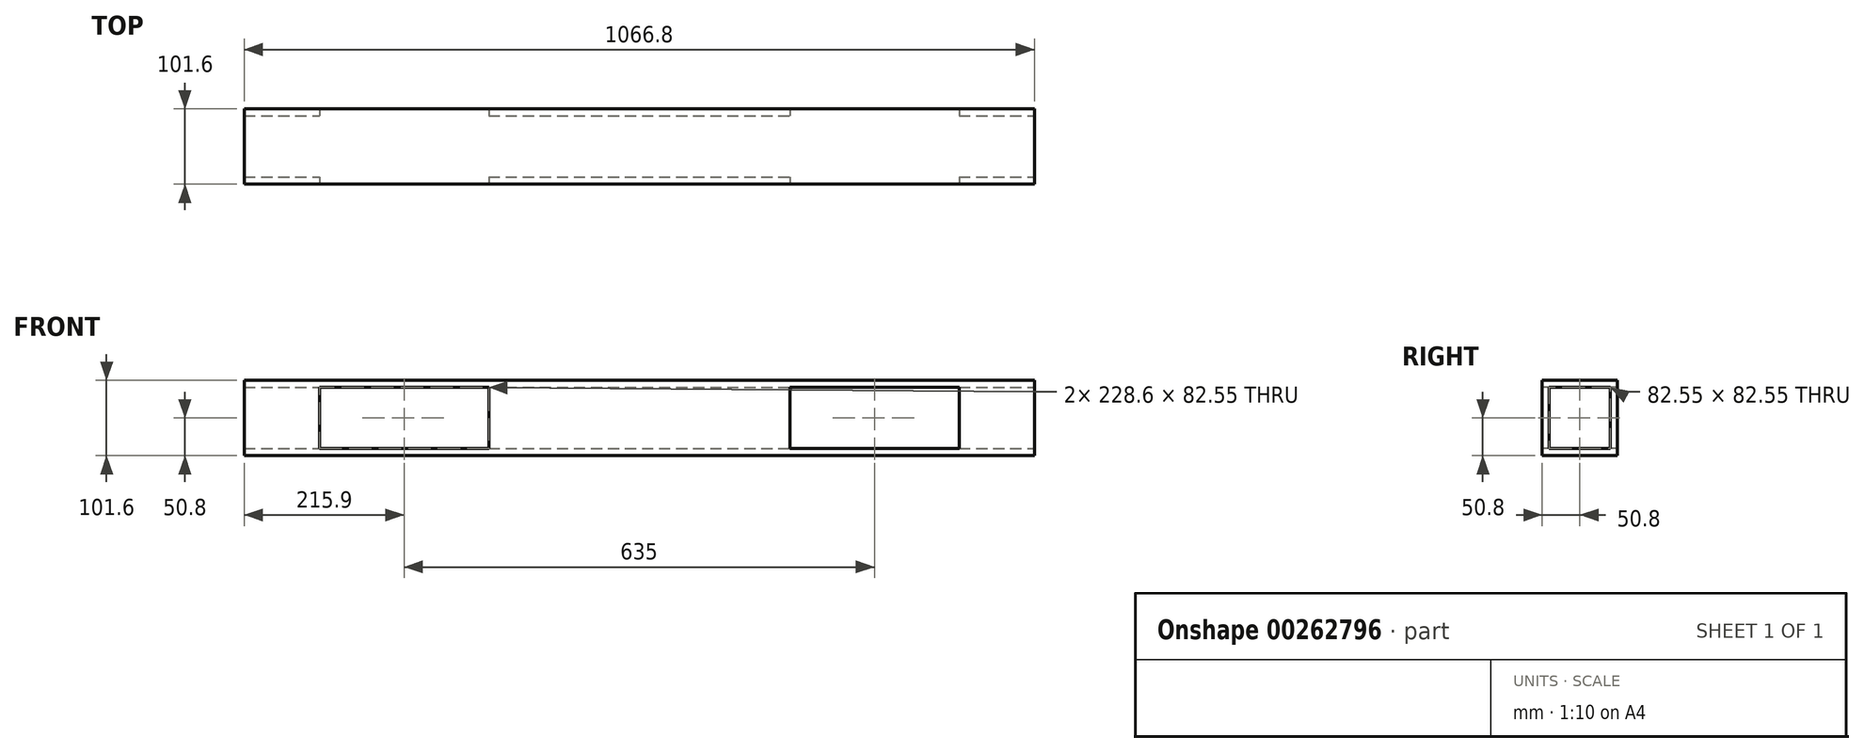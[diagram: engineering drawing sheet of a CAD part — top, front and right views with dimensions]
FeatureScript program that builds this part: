
annotation { "Feature Type Name" : "Feature", "Feature Type Description" : "" }
export const myFeature = defineFeature(function(context is Context, id is Id, definition is map)
    precondition{}
    {
        {
            var Q0;
            Q0=qCreatedBy(makeId("Top.planeOp"),FACE);
            var sketch = newSketch(context, id + "F0", { "sketchPlane" : qUnion([Q0])});
            skLineSegment(sketch, "E0.bottom", {"start": v(-533.4, -50.8) * mm, "end": v(533.4, -50.8) * mm});
            skLineSegment(sketch, "E0.top", {"start": v(-533.4, 50.8) * mm, "end": v(533.4, 50.8) * mm});
            skLineSegment(sketch, "E0.left", {"start": v(-533.4, -50.8) * mm, "end": v(-533.4, 50.8) * mm});
            skLineSegment(sketch, "E0.right", {"start": v(533.4, -50.8) * mm, "end": v(533.4, 50.8) * mm});
            skPoint(sketch, "E0.middle", {"position": v(0, 0) * mm});
            skSolve(sketch);
        }
        {
            var Q0;
            Q0=makeQuery(id+"F0.imprint","IMPRINT",FACE,{"disambiguationData":[TD([[makeQuery(id+"F0.imprint","IMPRINT",EDGE,{"derivedFrom":sQuery(id+"F0.wireOp",EDGE,"E0.bottom")}),1.0]])]});
            extrude(context, id + "F1", {"entities" : qUnion([Q0]), "endBound" : BoundingType.SYMMETRIC, "depth" : 101.6 * mm});
        }
        {
            var Q0;
            Q0=makeQuery(id+"F1.opExtrude","SWEPT_FACE",FACE,{"disambiguationData":[OSD([sQuery(id+"F0.wireOp",EDGE,"E0.right")])]});
            var sketch = newSketch(context, id + "F2", { "sketchPlane" : qUnion([Q0])});
            skLineSegment(sketch, "E1.0", {"start": v(-41.28, 41.28) * mm, "end": v(41.27, 41.28) * mm});
            skLineSegment(sketch, "E1.1", {"start": v(-41.28, 41.28) * mm, "end": v(-41.28, -41.28) * mm});
            skLineSegment(sketch, "E1.2", {"start": v(-41.28, -41.28) * mm, "end": v(41.27, -41.28) * mm});
            skLineSegment(sketch, "E1.3", {"start": v(41.27, 41.28) * mm, "end": v(41.27, -41.28) * mm});
            skSolve(sketch);
        }
        {
            var Q0;
            Q0=makeQuery(id+"F2.imprint","IMPRINT",FACE,{"disambiguationData":[TD([[makeQuery(id+"F2.imprint","IMPRINT",EDGE,{"derivedFrom":sQuery(id+"F2.wireOp",EDGE,"E1.0")}),-1.0]])]});
            extrude(context, id + "F3", {"entities" : qUnion([Q0]), "operationType" : NewBodyOperationType.REMOVE, "endBound" : BoundingType.THROUGH_ALL, "oppositeDirection" : true, "depth" : 25.4 * mm});
        }
        {
            var Q0;
            Q0=makeQuery(id+"F1.opExtrude","SWEPT_FACE",FACE,{"disambiguationData":[OSD([sQuery(id+"F0.wireOp",EDGE,"E0.bottom")])]});
            var sketch = newSketch(context, id + "F4", { "sketchPlane" : qUnion([Q0])});
            skLineSegment(sketch, "E2.bottom", {"start": v(-203.2, 50.8) * mm, "end": v(203.2, 50.8) * mm});
            skLineSegment(sketch, "E2.top", {"start": v(-203.2, -50.8) * mm, "end": v(203.2, -50.8) * mm});
            skLineSegment(sketch, "E2.left", {"start": v(-203.2, 50.8) * mm, "end": v(-203.2, -50.8) * mm});
            skLineSegment(sketch, "E2.right", {"start": v(203.2, 50.8) * mm, "end": v(203.2, -50.8) * mm});
            skPoint(sketch, "E2.middle", {"position": v(0, 0) * mm});
            skLineSegment(sketch, "E3.bottom", {"start": v(-203.2, -50.8) * mm, "end": v(-431.8, -50.8) * mm});
            skLineSegment(sketch, "E3.top", {"start": v(-203.2, 50.8) * mm, "end": v(-431.8, 50.8) * mm});
            skLineSegment(sketch, "E3.left", {"start": v(-203.2, -50.8) * mm, "end": v(-203.2, 50.8) * mm});
            skLineSegment(sketch, "E3.right", {"start": v(-431.8, -50.8) * mm, "end": v(-431.8, 50.8) * mm});
            skLineSegment(sketch, "E4.bottom", {"start": v(203.2, -50.8) * mm, "end": v(431.8, -50.8) * mm});
            skLineSegment(sketch, "E4.top", {"start": v(203.2, 50.8) * mm, "end": v(431.8, 50.8) * mm});
            skLineSegment(sketch, "E4.left", {"start": v(203.2, -50.8) * mm, "end": v(203.2, 50.8) * mm});
            skLineSegment(sketch, "E4.right", {"start": v(431.8, -50.8) * mm, "end": v(431.8, 50.8) * mm});
            skLineSegment(sketch, "E5.0", {"start": v(-203.2, 41.28) * mm, "end": v(-431.8, 41.28) * mm});
            skLineSegment(sketch, "E5.2", {"start": v(-203.2, -41.28) * mm, "end": v(-431.8, -41.28) * mm});
            skLineSegment(sketch, "E6.1", {"start": v(203.2, -41.27) * mm, "end": v(431.8, -41.27) * mm});
            skLineSegment(sketch, "E6.3", {"start": v(203.2, 41.27) * mm, "end": v(431.8, 41.27) * mm});
            skSolve(sketch);
        }
        {
            var Q0;
            {var subQ0=sQuery(id+"F4.wireOp",EDGE,"E5.0");Q0=makeQuery(id+"F4.imprint","IMPRINT",FACE,{"disambiguationData":[TD([[makeQuery(id+"F4.imprint","IMPRINT",EDGE,{"derivedFrom":subQ0}),1.0]])]});}
            var Q1;
            {var subQ0=sQuery(id+"F4.wireOp",EDGE,"E6.1");Q1=makeQuery(id+"F4.imprint","IMPRINT",FACE,{"disambiguationData":[TD([[makeQuery(id+"F4.imprint","IMPRINT",EDGE,{"derivedFrom":subQ0}),1.0]])]});}
            extrude(context, id + "F5", {"entities" : qUnion([Q0, Q1]), "operationType" : NewBodyOperationType.REMOVE, "endBound" : BoundingType.THROUGH_ALL, "oppositeDirection" : true, "depth" : 25.4 * mm});
        }
    });
